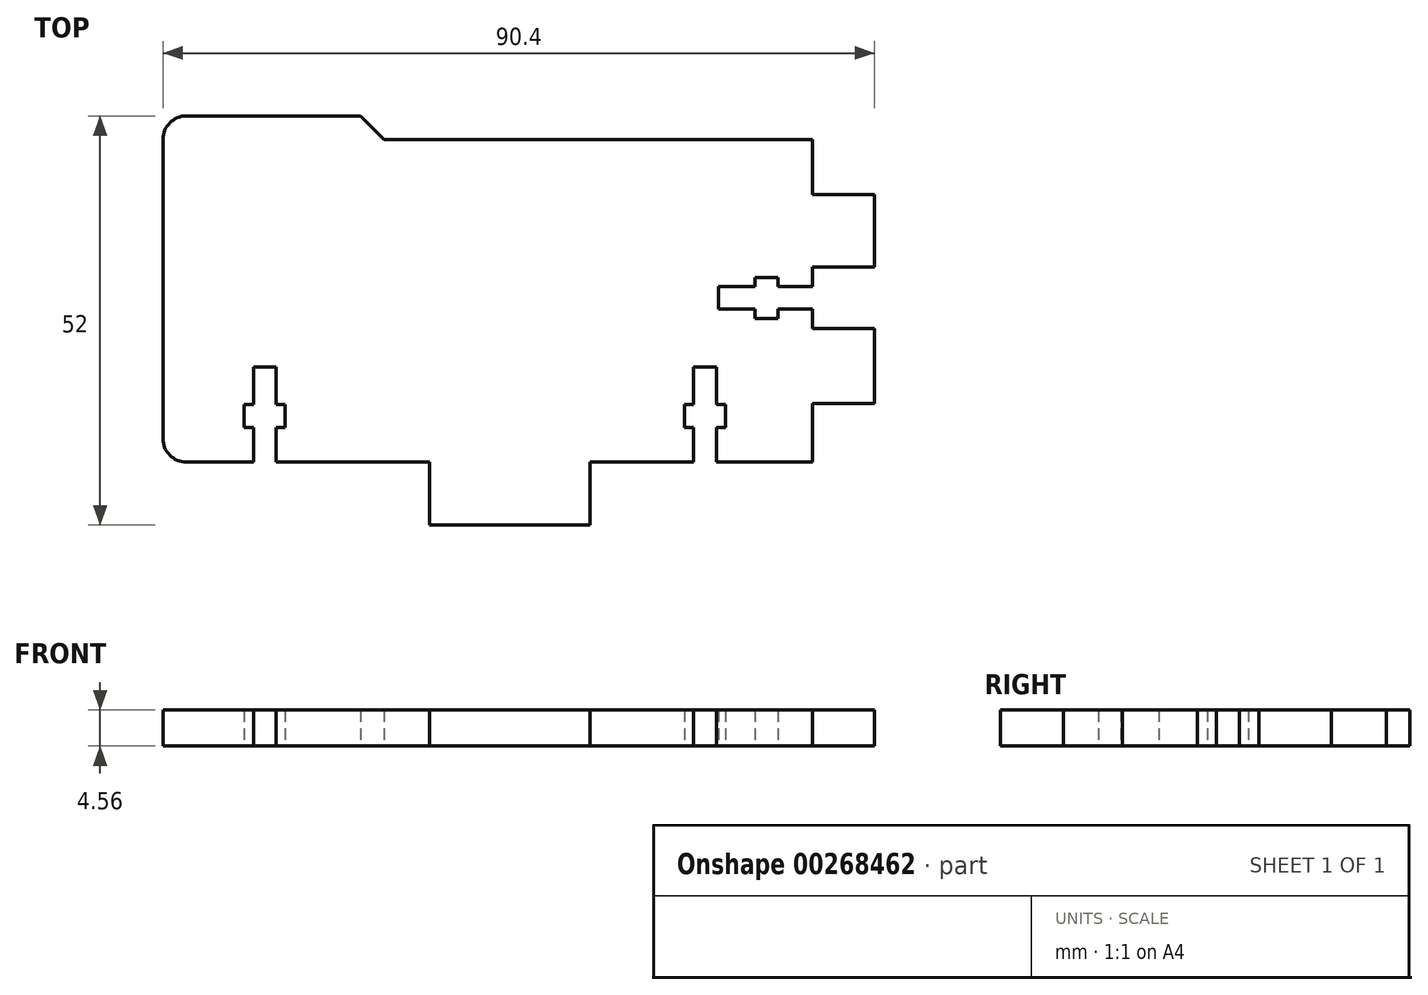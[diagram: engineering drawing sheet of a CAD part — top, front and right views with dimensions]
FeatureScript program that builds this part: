
annotation { "Feature Type Name" : "Feature", "Feature Type Description" : "" }
export const myFeature = defineFeature(function(context is Context, id is Id, definition is map)
    precondition{}
    {
        {
            var Q0;
            Q0=qCreatedBy(makeId("Top.planeOp"),FACE);
            var sketch = newSketch(context, id + "F0", { "sketchPlane" : qUnion([Q0])});
            skLineSegment(sketch, "E0", {"start": v(0, 0) * mm, "end": v(0, -8) * mm});
            skLineSegment(sketch, "E1", {"start": v(0, -8) * mm, "end": v(20.4, -8) * mm});
            skLineSegment(sketch, "E2", {"start": v(20.4, -8) * mm, "end": v(20.4, 0) * mm});
            skLineSegment(sketch, "E3", {"start": v(20.4, 0) * mm, "end": v(33.54, 0) * mm});
            skLineSegment(sketch, "E4", {"start": v(33.54, 0) * mm, "end": v(33.54, 4.4) * mm});
            skLineSegment(sketch, "E5", {"start": v(33.54, 4.4) * mm, "end": v(32.39, 4.4) * mm});
            skLineSegment(sketch, "E6", {"start": v(32.39, 4.4) * mm, "end": v(32.39, 7.3) * mm});
            skLineSegment(sketch, "E7", {"start": v(32.39, 7.3) * mm, "end": v(33.54, 7.3) * mm});
            skLineSegment(sketch, "E8", {"start": v(33.54, 7.3) * mm, "end": v(33.54, 12.1) * mm});
            skLineSegment(sketch, "E9", {"start": v(33.54, 12.1) * mm, "end": v(36.44, 12.1) * mm});
            skLineSegment(sketch, "E10", {"start": v(36.44, 12.1) * mm, "end": v(36.44, 7.3) * mm});
            skLineSegment(sketch, "E11", {"start": v(36.44, 7.3) * mm, "end": v(37.59, 7.3) * mm});
            skLineSegment(sketch, "E12", {"start": v(37.59, 7.3) * mm, "end": v(37.59, 4.4) * mm});
            skLineSegment(sketch, "E13", {"start": v(37.59, 4.4) * mm, "end": v(36.44, 4.4) * mm});
            skLineSegment(sketch, "E14", {"start": v(36.44, 4.4) * mm, "end": v(36.44, 0) * mm});
            skLineSegment(sketch, "E15", {"start": v(36.44, 0) * mm, "end": v(48.64, 0) * mm});
            skLineSegment(sketch, "E16", {"start": v(48.64, 0) * mm, "end": v(48.64, 7.48) * mm});
            skLineSegment(sketch, "E17", {"start": v(48.64, 7.48) * mm, "end": v(56.54, 7.48) * mm});
            skLineSegment(sketch, "E18", {"start": v(56.54, 7.48) * mm, "end": v(56.54, 16.98) * mm});
            skLineSegment(sketch, "E19", {"start": v(56.54, 16.98) * mm, "end": v(48.64, 16.98) * mm});
            skLineSegment(sketch, "E20", {"start": v(48.64, 16.98) * mm, "end": v(48.64, 19.43) * mm});
            skLineSegment(sketch, "E21", {"start": v(48.64, 19.43) * mm, "end": v(44.24, 19.43) * mm});
            skLineSegment(sketch, "E22", {"start": v(44.24, 19.43) * mm, "end": v(44.24, 18.28) * mm});
            skLineSegment(sketch, "E23", {"start": v(44.24, 18.28) * mm, "end": v(41.34, 18.28) * mm});
            skLineSegment(sketch, "E24", {"start": v(41.34, 18.28) * mm, "end": v(41.34, 19.43) * mm});
            skLineSegment(sketch, "E25", {"start": v(41.34, 19.43) * mm, "end": v(36.68, 19.43) * mm});
            skLineSegment(sketch, "E26", {"start": v(36.68, 19.43) * mm, "end": v(36.68, 22.33) * mm});
            skLineSegment(sketch, "E27", {"start": v(36.68, 22.33) * mm, "end": v(41.34, 22.33) * mm});
            skLineSegment(sketch, "E28", {"start": v(41.34, 22.33) * mm, "end": v(41.34, 23.48) * mm});
            skLineSegment(sketch, "E29", {"start": v(41.34, 23.48) * mm, "end": v(44.24, 23.48) * mm});
            skLineSegment(sketch, "E30", {"start": v(44.24, 23.48) * mm, "end": v(44.24, 22.33) * mm});
            skLineSegment(sketch, "E31", {"start": v(44.24, 22.33) * mm, "end": v(48.64, 22.33) * mm});
            skLineSegment(sketch, "E32", {"start": v(48.64, 22.33) * mm, "end": v(48.64, 24.78) * mm});
            skLineSegment(sketch, "E33", {"start": v(48.64, 24.78) * mm, "end": v(56.54, 24.78) * mm});
            skLineSegment(sketch, "E34", {"start": v(56.54, 24.78) * mm, "end": v(56.54, 34) * mm});
            skLineSegment(sketch, "E35", {"start": v(56.54, 34) * mm, "end": v(48.64, 34) * mm});
            skLineSegment(sketch, "E36", {"start": v(48.64, 34) * mm, "end": v(48.64, 41) * mm});
            skLineSegment(sketch, "E37", {"start": v(48.64, 41) * mm, "end": v(-5.76, 41) * mm});
            skLineSegment(sketch, "E38", {"start": v(-5.76, 41) * mm, "end": v(-8.76, 44) * mm});
            skLineSegment(sketch, "E39", {"start": v(-8.76, 44) * mm, "end": v(-30.86, 44) * mm});
            skLineSegment(sketch, "E40", {"start": v(-33.86, 41) * mm, "end": v(-33.86, 3) * mm});
            skLineSegment(sketch, "E41", {"start": v(-30.86, 0) * mm, "end": v(-22.38, 0) * mm});
            skLineSegment(sketch, "E42", {"start": v(-22.38, 0) * mm, "end": v(-22.38, 4.4) * mm});
            skLineSegment(sketch, "E43", {"start": v(-22.38, 4.4) * mm, "end": v(-23.53, 4.4) * mm});
            skLineSegment(sketch, "E44", {"start": v(-23.53, 4.4) * mm, "end": v(-23.53, 7.3) * mm});
            skLineSegment(sketch, "E45", {"start": v(-23.53, 7.3) * mm, "end": v(-22.38, 7.3) * mm});
            skLineSegment(sketch, "E46", {"start": v(-22.38, 7.3) * mm, "end": v(-22.38, 12.1) * mm});
            skLineSegment(sketch, "E47", {"start": v(-22.38, 12.1) * mm, "end": v(-19.48, 12.1) * mm});
            skLineSegment(sketch, "E48", {"start": v(-19.48, 12.1) * mm, "end": v(-19.48, 7.3) * mm});
            skLineSegment(sketch, "E49", {"start": v(-19.48, 7.3) * mm, "end": v(-18.33, 7.3) * mm});
            skLineSegment(sketch, "E50", {"start": v(-18.33, 7.3) * mm, "end": v(-18.33, 4.4) * mm});
            skLineSegment(sketch, "E51", {"start": v(-18.33, 4.4) * mm, "end": v(-19.48, 4.4) * mm});
            skLineSegment(sketch, "E52", {"start": v(-19.48, 4.4) * mm, "end": v(-19.48, 0) * mm});
            skLineSegment(sketch, "E53", {"start": v(-19.48, 0) * mm, "end": v(0, 0) * mm});
            skPoint(sketch, "E54.visualSharp", {"position": v(-33.86, 44) * mm});
            skArc(sketch, "E54.filletArc", {"start": v(-30.86, 44) * mm, "mid": v(-32.98, 43.12) * mm, "end": v(-33.86, 41) * mm});
            skPoint(sketch, "E55.visualSharp", {"position": v(-33.86, 0) * mm});
            skArc(sketch, "E55.filletArc", {"start": v(-33.86, 3) * mm, "mid": v(-32.98, 0.88) * mm, "end": v(-30.86, 0) * mm});
            skSolve(sketch);
        }
        {
            var Q0;
            Q0=makeQuery(id+"F0.imprint","IMPRINT",FACE,{"disambiguationData":[TD([[makeQuery(id+"F0.imprint","IMPRINT",EDGE,{"derivedFrom":sQuery(id+"F0.wireOp",EDGE,"E0")}),1.0]])]});
            extrude(context, id + "F1", {"entities" : qUnion([Q0]), "depth" : 4.56 * mm});
        }
    });
